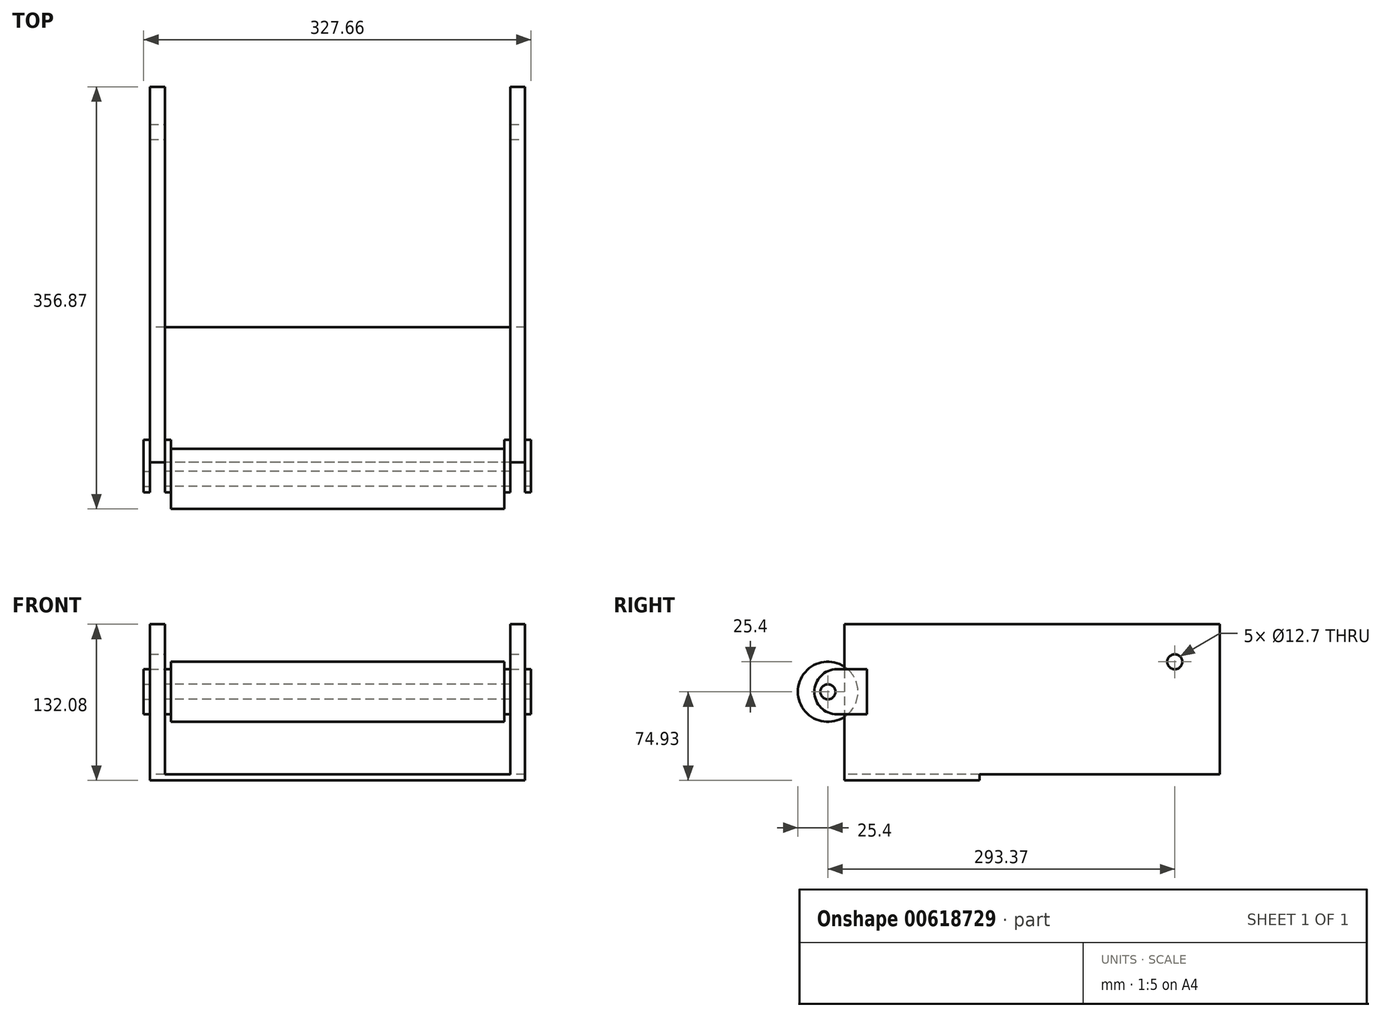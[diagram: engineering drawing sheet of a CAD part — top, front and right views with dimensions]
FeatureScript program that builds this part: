
annotation { "Feature Type Name" : "Feature", "Feature Type Description" : "" }
export const myFeature = defineFeature(function(context is Context, id is Id, definition is map)
    precondition{}
    {
        {
            var Q0;
            Q0=qCreatedBy(makeId("Right.planeOp"),FACE);
            var sketch = newSketch(context, id + "F0", { "sketchPlane" : qUnion([Q0])});
            skLineSegment(sketch, "E0.bottom", {"start": v(57.15, 2.54) * mm, "end": v(-57.15, 2.54) * mm});
            skLineSegment(sketch, "E0.top", {"start": v(57.15, -2.54) * mm, "end": v(-57.15, -2.54) * mm});
            skLineSegment(sketch, "E0.left", {"start": v(57.15, 2.54) * mm, "end": v(57.15, -2.54) * mm});
            skLineSegment(sketch, "E0.right", {"start": v(-57.15, 2.54) * mm, "end": v(-57.15, -2.54) * mm});
            skPoint(sketch, "E0.middle", {"position": v(0, 0) * mm});
            skSolve(sketch);
        }
        {
            var Q0;
            Q0 = qSketchRegion(id + "F0", true);
            extrude(context, id + "F1", {"entities" : qUnion([Q0]), "endBound" : BoundingType.SYMMETRIC, "depth" : 317.5 * mm, "offsetDistance" : 25.4 * mm});
        }
        {
            var Q0;
            Q0=makeQuery(id+"F1.opExtrude","SWEPT_FACE",FACE,{"disambiguationData":[OSD([sQuery(id+"F0.wireOp",EDGE,"E0.bottom")])]});
            var sketch = newSketch(context, id + "F2", { "sketchPlane" : qUnion([Q0])});
            skLineSegment(sketch, "E1.bottom", {"start": v(146.05, 260.35) * mm, "end": v(158.75, 260.35) * mm});
            skLineSegment(sketch, "E1.top", {"start": v(146.05, -57.15) * mm, "end": v(158.75, -57.15) * mm});
            skLineSegment(sketch, "E1.left", {"start": v(146.05, 260.35) * mm, "end": v(146.05, -57.15) * mm});
            skLineSegment(sketch, "E1.right", {"start": v(158.75, 260.35) * mm, "end": v(158.75, -57.15) * mm});
            skLineSegment(sketch, "E2.MirrorCS", {"start": v(-146.05, 260.35) * mm, "end": v(-146.05, -57.15) * mm});
            skLineSegment(sketch, "E3.MirrorCS", {"start": v(-158.75, 260.35) * mm, "end": v(-158.75, -57.15) * mm});
            skLineSegment(sketch, "E4.MirrorCS", {"start": v(-146.05, -57.15) * mm, "end": v(-158.75, -57.15) * mm});
            skLineSegment(sketch, "E5.MirrorCS", {"start": v(-146.05, 260.35) * mm, "end": v(-158.75, 260.35) * mm});
            skSolve(sketch);
        }
        {
            var Q0;
            Q0 = qSketchRegion(id + "F2", true);
            extrude(context, id + "F3", {"entities" : qUnion([Q0]), "operationType" : NewBodyOperationType.ADD, "depth" : 127 * mm, "offsetDistance" : 25.4 * mm});
        }
        {
            var Q0;
            Q0=makeQuery(id+"F3.opExtrude","SWEPT_FACE",FACE,{"disambiguationData":[OSD([sQuery(id+"F2.wireOp",EDGE,"E2.MirrorCS")])]});
            var sketch = newSketch(context, id + "F4", { "sketchPlane" : qUnion([Q0])});
            skLineSegment(sketch, "E6.bottom", {"start": v(-63.5, 91.44) * mm, "end": v(-38.1, 91.44) * mm});
            skLineSegment(sketch, "E6.top", {"start": v(-63.5, 53.34) * mm, "end": v(-38.1, 53.34) * mm});
            skLineSegment(sketch, "E6.right", {"start": v(-38.1, 91.44) * mm, "end": v(-38.1, 53.34) * mm});
            skArc(sketch, "E7", {"start": v(-63.5, 91.44) * mm, "mid": v(-82.55, 72.4) * mm, "end": v(-63.5, 53.34) * mm});
            skCircle(sketch, "E8", {"center": v(-71.12, 72.4) * mm, "radius": 6.35 * mm});
            skSolve(sketch);
        }
        {
            var Q0;
            Q0 = qSketchRegion(id + "F4", true);
            extrude(context, id + "F5", {"entities" : qUnion([Q0]), "operationType" : NewBodyOperationType.ADD, "depth" : 5.08 * mm, "offsetDistance" : 25.4 * mm});
        }
        {
            var Q0;
            Q0=makeQuery(id+"F3.boolean.opBoolean","MERGE",FACE,{"derivedFrom":[makeQuery(id+"F1.opExtrude","CAP_FACE",FACE,{"disambiguationData":[OSD([sQuery(id+"F0.wireOp",EDGE,"E0.bottom"),sQuery(id+"F0.wireOp",EDGE,"E0.top"),sQuery(id+"F0.wireOp",EDGE,"E0.left"),sQuery(id+"F0.wireOp",EDGE,"E0.right")])],"isStart":true}),makeQuery(id+"F3.opExtrude","SWEPT_FACE",FACE,{"disambiguationData":[OSD([sQuery(id+"F2.wireOp",EDGE,"E3.MirrorCS")])]})]});
            var sketch = newSketch(context, id + "F6", { "sketchPlane" : qUnion([Q0])});
            skLineSegment(sketch, "E9.bottom", {"start": v(38.1, 91.44) * mm, "end": v(63.5, 91.44) * mm});
            skLineSegment(sketch, "E9.top", {"start": v(38.1, 53.34) * mm, "end": v(63.5, 53.34) * mm});
            skLineSegment(sketch, "E9.left", {"start": v(38.1, 91.44) * mm, "end": v(38.1, 53.34) * mm});
            skArc(sketch, "E10", {"start": v(63.5, 53.34) * mm, "mid": v(82.55, 72.39) * mm, "end": v(63.5, 91.44) * mm});
            skCircle(sketch, "E11", {"center": v(71.12, 72.39) * mm, "radius": 6.35 * mm});
            skSolve(sketch);
        }
        {
            var Q0;
            Q0 = qSketchRegion(id + "F6", true);
            extrude(context, id + "F7", {"entities" : qUnion([Q0]), "operationType" : NewBodyOperationType.ADD, "depth" : 5.08 * mm, "offsetDistance" : 25.4 * mm});
        }
        {
            var Q0;
            Q0=makeQuery(id+"F1.opExtrude","SWEPT_BODY",BODY,{"disambiguationData":[OSD([sQuery(id+"F0.wireOp",EDGE,"E0.bottom"),sQuery(id+"F0.wireOp",EDGE,"E0.top"),sQuery(id+"F0.wireOp",EDGE,"E0.left"),sQuery(id+"F0.wireOp",EDGE,"E0.right")])]});
            var Q1;
            Q1=qCreatedBy(makeId("Right.planeOp"),FACE);
            mirror(context, id + "F8", {"operationType" : NewBodyOperationType.ADD, "entities" : qUnion([Q0]), "mirrorPlane" : qUnion([Q1])});
        }
        {
            var Q0;
            Q0=makeQuery(id+"F5.opExtrude","CAP_FACE",FACE,{"disambiguationData":[OSD([sQuery(id+"F4.wireOp",EDGE,"E6.bottom"),sQuery(id+"F4.wireOp",EDGE,"E6.top"),sQuery(id+"F4.wireOp",EDGE,"E6.right"),sQuery(id+"F4.wireOp",EDGE,"E7"),sQuery(id+"F4.wireOp",EDGE,"E8")])],"isStart":false});
            var sketch = newSketch(context, id + "F9", { "sketchPlane" : qUnion([Q0])});
            skCircle(sketch, "E12", {"center": v(-71.12, 72.4) * mm, "radius": 25.4 * mm});
            skSolve(sketch);
        }
        {
            var Q0;
            Q0 = qSketchRegion(id + "F9", true);
            extrude(context, id + "F10", {"entities" : qUnion([Q0]), "operationType" : NewBodyOperationType.ADD, "depth" : 281.94 * mm, "offsetDistance" : 25.4 * mm});
        }
        {
            var Q0;
            Q0=makeQuery(id+"F8.opPattern","COPY",FACE,{"derivedFrom":makeQuery(id+"F7.opExtrude","CAP_FACE",FACE,{"disambiguationData":[OSD([sQuery(id+"F6.wireOp",EDGE,"E9.bottom"),sQuery(id+"F6.wireOp",EDGE,"E9.top"),sQuery(id+"F6.wireOp",EDGE,"E9.left"),sQuery(id+"F6.wireOp",EDGE,"E10"),sQuery(id+"F6.wireOp",EDGE,"E11")])],"isStart":false}),"instanceName":"1"});
            var sketch = newSketch(context, id + "F11", { "sketchPlane" : qUnion([Q0])});
            skCircle(sketch, "E13", {"center": v(-71.12, 72.39) * mm, "radius": 6.35 * mm});
            skSolve(sketch);
        }
        {
            var Q0;
            Q0 = qSketchRegion(id + "F11", true);
            extrude(context, id + "F12", {"entities" : qUnion([Q0]), "operationType" : NewBodyOperationType.REMOVE, "oppositeDirection" : true, "depth" : 327.66 * mm, "offsetDistance" : 25.4 * mm});
        }
        {
            var Q0;
            Q0=makeQuery(id+"F3.boolean.opBoolean","MERGE",FACE,{"derivedFrom":[makeQuery(id+"F1.opExtrude","CAP_FACE",FACE,{"disambiguationData":[OSD([sQuery(id+"F0.wireOp",EDGE,"E0.bottom"),sQuery(id+"F0.wireOp",EDGE,"E0.top"),sQuery(id+"F0.wireOp",EDGE,"E0.left"),sQuery(id+"F0.wireOp",EDGE,"E0.right")])],"isStart":false}),makeQuery(id+"F3.opExtrude","SWEPT_FACE",FACE,{"disambiguationData":[OSD([sQuery(id+"F2.wireOp",EDGE,"E1.right")])]})]});
            var sketch = newSketch(context, id + "F13", { "sketchPlane" : qUnion([Q0])});
            skCircle(sketch, "E14", {"center": v(222.25, 97.8) * mm, "radius": 6.35 * mm});
            skSolve(sketch);
        }
        {
            var Q0;
            Q0 = qSketchRegion(id + "F13", true);
            extrude(context, id + "F14", {"entities" : qUnion([Q0]), "operationType" : NewBodyOperationType.REMOVE, "endBound" : BoundingType.THROUGH_ALL, "oppositeDirection" : true, "depth" : 25.4 * mm, "offsetDistance" : 25.4 * mm});
        }
    });
